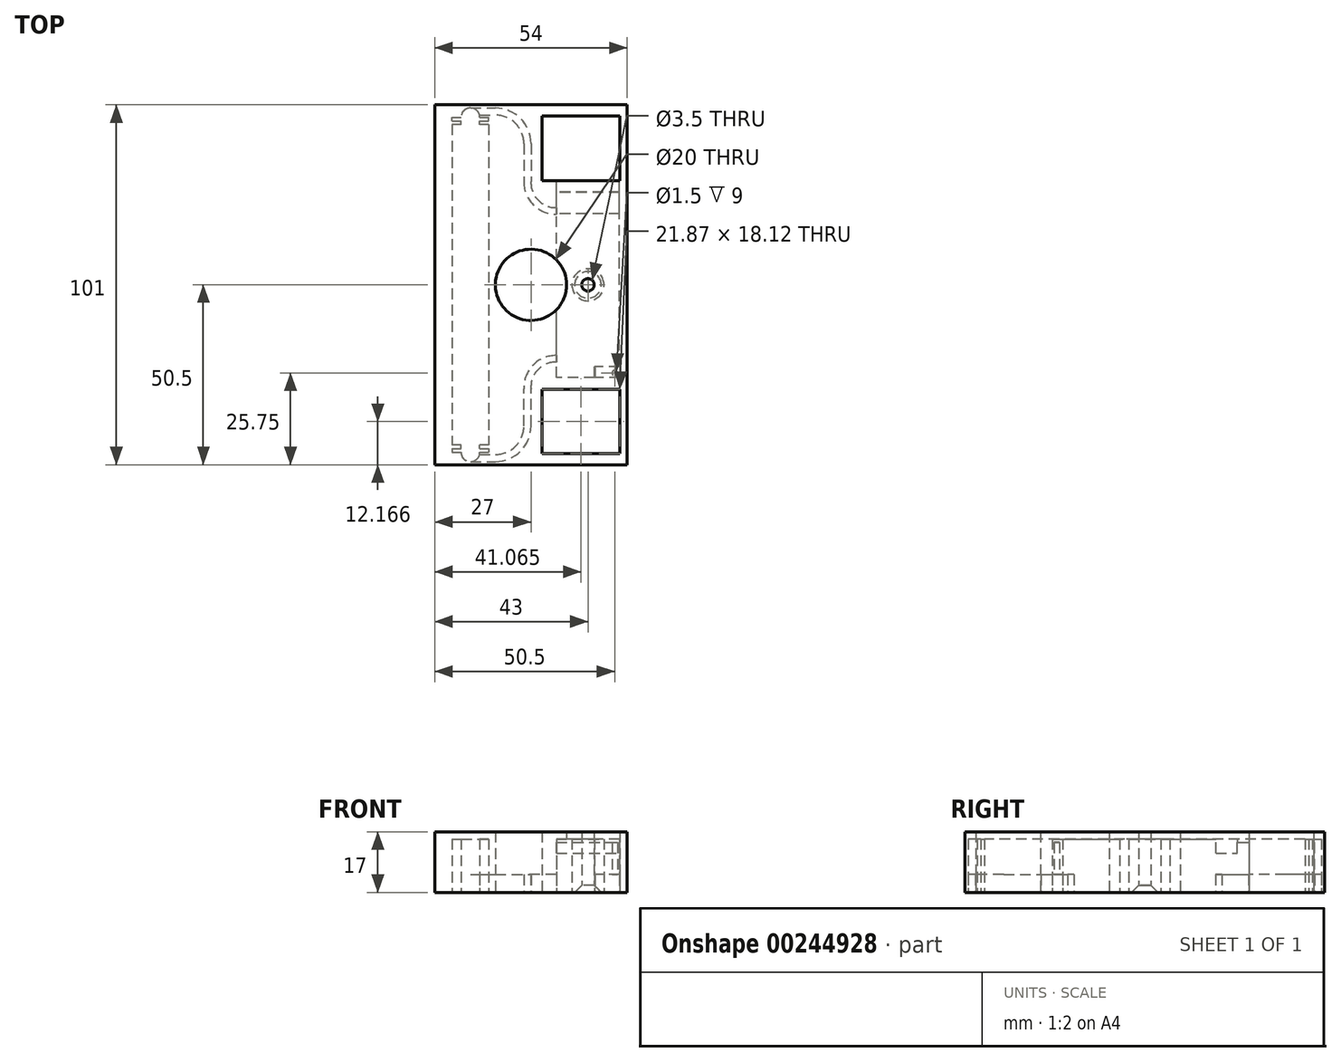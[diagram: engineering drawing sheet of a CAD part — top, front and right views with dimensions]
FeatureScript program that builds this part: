
annotation { "Feature Type Name" : "Feature", "Feature Type Description" : "" }
export const myFeature = defineFeature(function(context is Context, id is Id, definition is map)
    precondition{}
    {
        {
            var Q0;
            Q0=qCreatedBy(makeId("Top.planeOp"),FACE);
            var sketch = newSketch(context, id + "F0", { "sketchPlane" : qUnion([Q0])});
            skPoint(sketch, "E0.middle", {"position": v(0, 0) * mm});
            skLineSegment(sketch, "E1.bottom", {"start": v(27, 50.5) * mm, "end": v(-27, 50.5) * mm});
            skLineSegment(sketch, "E1.top", {"start": v(27, -50.5) * mm, "end": v(-27, -50.5) * mm});
            skLineSegment(sketch, "E1.left", {"start": v(27, 50.5) * mm, "end": v(27, -50.5) * mm});
            skLineSegment(sketch, "E2", {"start": v(-27, -50.5) * mm, "end": v(-27, 50.5) * mm});
            skLineSegment(sketch, "E3.bottom", {"start": v(25, -29.27) * mm, "end": v(3.13, -29.27) * mm});
            skLineSegment(sketch, "E3.top", {"start": v(25, -47.4) * mm, "end": v(3.13, -47.4) * mm});
            skLineSegment(sketch, "E3.left", {"start": v(25, -29.27) * mm, "end": v(25, -47.4) * mm});
            skLineSegment(sketch, "E3.right", {"start": v(3.13, -29.27) * mm, "end": v(3.13, -47.4) * mm});
            skPoint(sketch, "E3.middle", {"position": v(14.07, -38.33) * mm});
            skLineSegment(sketch, "E4", {"start": v(25, -38.33) * mm, "end": v(27, -38.33) * mm});
            skPoint(sketch, "E5.MirrorP", {"position": v(14.07, 38.33) * mm});
            skLineSegment(sketch, "E6.MirrorCS", {"start": v(25, 47.4) * mm, "end": v(3.13, 47.4) * mm});
            skLineSegment(sketch, "E7.MirrorCS", {"start": v(3.13, 29.27) * mm, "end": v(3.13, 47.4) * mm});
            skLineSegment(sketch, "E8.MirrorCS", {"start": v(25, 29.27) * mm, "end": v(3.13, 29.27) * mm});
            skLineSegment(sketch, "E9.MirrorCS", {"start": v(25, 29.27) * mm, "end": v(25, 47.4) * mm});
            skCircle(sketch, "E10", {"center": v(0, 0) * mm, "radius": 10 * mm});
            skLineSegment(sketch, "E11", {"start": v(0, 0) * mm, "end": v(16, 0) * mm});
            skCircle(sketch, "E12", {"center": v(16, 0) * mm, "radius": 1.75 * mm});
            skLineSegment(sketch, "E13", {"start": v(0, -15) * mm, "end": v(2, -15) * mm});
            skSolve(sketch);
        }
        {
            var Q0;
            Q0 = qSketchRegion(id + "F0", true);
            extrude(context, id + "F1", {"entities" : qUnion([Q0]), "depth" : 17 * mm});
        }
        {
            var Q0;
            Q0=makeQuery(id+"F1.opExtrude","CAP_FACE",FACE,{"disambiguationData":[OSD([sQuery(id+"F0.wireOp",EDGE,"E1.bottom"),sQuery(id+"F0.wireOp",EDGE,"E1.top"),sQuery(id+"F0.wireOp",EDGE,"E1.left"),sQuery(id+"F0.wireOp",EDGE,"E1.right")])],"isStart":true});
            var sketch = newSketch(context, id + "F2", { "sketchPlane" : qUnion([Q0])});
            skLineSegment(sketch, "E14", {"start": v(0, 0) * mm, "end": v(16, 0) * mm});
            skLineSegment(sketch, "E15.bottom", {"start": v(17.87, 26) * mm, "end": v(7.12, 26) * mm});
            skLineSegment(sketch, "E15.top", {"start": v(24.87, -26) * mm, "end": v(7.13, -26) * mm});
            skLineSegment(sketch, "E15.left", {"start": v(24.87, 23) * mm, "end": v(24.87, -26) * mm});
            skPoint(sketch, "E15.middle", {"position": v(16, 0) * mm});
            skCircle(sketch, "E16", {"center": v(16, 0) * mm, "radius": 4.5 * mm});
            skLineSegment(sketch, "E17.top", {"start": v(24.87, 23) * mm, "end": v(17.87, 23) * mm});
            skLineSegment(sketch, "E17.right", {"start": v(17.87, 26) * mm, "end": v(17.87, 23) * mm});
            skPoint(sketch, "E17.left.start.orphan", {"position": v(24.87, 26) * mm});
            skLineSegment(sketch, "E18.bottom", {"start": v(-11.86, -45) * mm, "end": v(-14.36, -45) * mm});
            skLineSegment(sketch, "E18.top", {"start": v(-11.86, 45) * mm, "end": v(-14.36, 45) * mm});
            skLineSegment(sketch, "E18.left", {"start": v(-11.86, -45) * mm, "end": v(-11.86, 45) * mm});
            skLineSegment(sketch, "E18.right", {"start": v(-22.14, -45) * mm, "end": v(-22.14, 45) * mm});
            skPoint(sketch, "E18.middle", {"position": v(-17, 0) * mm});
            skLineSegment(sketch, "E19", {"start": v(0, 0) * mm, "end": v(-17, 0) * mm});
            skPoint(sketch, "E20.middle", {"position": v(-17, 45) * mm});
            skLineSegment(sketch, "E21.bottom", {"start": v(-22.14, 46) * mm, "end": v(-19.64, 46) * mm});
            skLineSegment(sketch, "E21.top", {"start": v(-22.14, 47) * mm, "end": v(-19.64, 47) * mm});
            skLineSegment(sketch, "E21.left", {"start": v(-22.14, 46) * mm, "end": v(-22.14, 47) * mm});
            skLineSegment(sketch, "E21.right", {"start": v(-11.84, 46) * mm, "end": v(-11.84, 47) * mm});
            skArc(sketch, "E22", {"start": v(-14.36, 47) * mm, "mid": v(-17, 49.64) * mm, "end": v(-19.64, 47) * mm});
            skLineSegment(sketch, "E23.trimOffspring", {"start": v(-19.64, 45) * mm, "end": v(-22.14, 45) * mm});
            skLineSegment(sketch, "E24.trimOffspring", {"start": v(-14.36, 46) * mm, "end": v(-11.84, 46) * mm});
            skLineSegment(sketch, "E25.trimOffspring", {"start": v(-14.36, 47) * mm, "end": v(-11.84, 47) * mm});
            skLineSegment(sketch, "E26.MirrorCS", {"start": v(-14.36, -45) * mm, "end": v(-14.36, -46) * mm});
            skLineSegment(sketch, "E27.MirrorCS", {"start": v(-19.64, -45) * mm, "end": v(-19.64, -46) * mm});
            skLineSegment(sketch, "E28.MirrorCS", {"start": v(-22.14, -46) * mm, "end": v(-19.64, -46) * mm});
            skLineSegment(sketch, "E29.MirrorCS", {"start": v(-22.14, -46) * mm, "end": v(-22.14, -47) * mm});
            skLineSegment(sketch, "E30.MirrorCS", {"start": v(-22.14, -47) * mm, "end": v(-19.64, -47) * mm});
            skArc(sketch, "E31.MirrorCS", {"start": v(-14.36, -47) * mm, "mid": v(-17, -49.64) * mm, "end": v(-19.64, -47) * mm});
            skLineSegment(sketch, "E32.MirrorCS", {"start": v(-14.36, -47) * mm, "end": v(-11.84, -47) * mm});
            skLineSegment(sketch, "E33.MirrorCS", {"start": v(-11.84, -46) * mm, "end": v(-11.84, -47) * mm});
            skLineSegment(sketch, "E34.MirrorCS", {"start": v(-14.36, -46) * mm, "end": v(-11.84, -46) * mm});
            skLineSegment(sketch, "E35", {"start": v(7.12, 26) * mm, "end": v(7.13, -26) * mm});
            skLineSegment(sketch, "E36.trimOffspring", {"start": v(-19.64, -45) * mm, "end": v(-22.14, -45) * mm});
            skLineSegment(sketch, "E37", {"start": v(-19.64, 46) * mm, "end": v(-19.64, 45) * mm});
            skLineSegment(sketch, "E38", {"start": v(-14.36, 46) * mm, "end": v(-14.36, 45) * mm});
            skSolve(sketch);
        }
        {
            var Q0;
            Q0 = qSketchRegion(id + "F2", true);
            extrude(context, id + "F3", {"entities" : qUnion([Q0]), "operationType" : NewBodyOperationType.REMOVE, "oppositeDirection" : true, "depth" : 15 * mm});
        }
        {
            var Q0;
            {var subQ5=sQuery(id+"F0.wireOp",EDGE,"E1.top");var subQ6=sQuery(id+"F0.wireOp",EDGE,"E1.right");var subQ7=sQuery(id+"F0.wireOp",EDGE,"E1.bottom");var subQ8=sQuery(id+"F0.wireOp",EDGE,"E1.left");Q0=makeQuery(id+"F3.boolean.opBoolean","SPLIT",FACE,{"disambiguationData":[TD([makeQuery(id+"F1.opExtrude","SWEPT_FACE",FACE,{"disambiguationData":[OSD([subQ7])]})])],"derivedFrom":makeQuery(id+"F1.opExtrude","CAP_FACE",FACE,{"disambiguationData":[OSD([subQ7,subQ5,subQ8,subQ6])],"isStart":true})});}
            var sketch = newSketch(context, id + "F4", { "sketchPlane" : qUnion([Q0])});
            skLineSegment(sketch, "E39.bottom", {"start": v(25, 23) * mm, "end": v(18, 23) * mm});
            skLineSegment(sketch, "E39.top", {"start": v(25, 26) * mm, "end": v(18, 26) * mm});
            skLineSegment(sketch, "E39.left", {"start": v(25, 23) * mm, "end": v(25, 26) * mm});
            skLineSegment(sketch, "E39.right", {"start": v(18, 23) * mm, "end": v(18, 26) * mm});
            skPoint(sketch, "E39.middle", {"position": v(21.5, 24.5) * mm});
            skPoint(sketch, "E40.startSnap0", {"position": v(-17, 49.64) * mm});
            skArc(sketch, "E41", {"start": v(0, 39.62) * mm, "mid": v(-2.93, 46.7) * mm, "end": v(-10, 49.62) * mm});
            skArc(sketch, "E42", {"start": v(0, 29.13) * mm, "mid": v(1.92, 23.83) * mm, "end": v(7.12, 21.66) * mm});
            skLineSegment(sketch, "E43", {"start": v(0, 39.62) * mm, "end": v(0, 29.13) * mm});
            skLineSegment(sketch, "E44", {"start": v(-2, 39.62) * mm, "end": v(-2, 29.13) * mm});
            skArc(sketch, "E45", {"start": v(-2, 29.13) * mm, "mid": v(0.58, 22.52) * mm, "end": v(7.16, 19.84) * mm});
            skPoint(sketch, "E46.MirrorP", {"position": v(-17, -49.64) * mm});
            skLineSegment(sketch, "E47", {"start": v(7.12, 21.66) * mm, "end": v(7.16, 19.84) * mm});
            skLineSegment(sketch, "E48", {"start": v(-17, 49.64) * mm, "end": v(-10, 49.62) * mm});
            skLineSegment(sketch, "E49", {"start": v(-10, 49.62) * mm, "end": v(0, 49.62) * mm});
            skLineSegment(sketch, "E50", {"start": v(-17, 49.64) * mm, "end": v(-17, 47.64) * mm});
            skLineSegment(sketch, "E51", {"start": v(-17, 47.64) * mm, "end": v(-10, 47.64) * mm});
            skArc(sketch, "E52", {"start": v(-2, 39.62) * mm, "mid": v(-4.34, 45.29) * mm, "end": v(-10, 47.64) * mm});
            skArc(sketch, "E53.MirrorCS", {"start": v(-2, -29.13) * mm, "mid": v(0.58, -22.52) * mm, "end": v(7.16, -19.84) * mm});
            skArc(sketch, "E54.MirrorCS", {"start": v(0, -29.13) * mm, "mid": v(1.92, -23.83) * mm, "end": v(7.12, -21.66) * mm});
            skLineSegment(sketch, "E55.MirrorCS", {"start": v(-2, -39.62) * mm, "end": v(-2, -29.13) * mm});
            skLineSegment(sketch, "E56.MirrorCS", {"start": v(0, -39.62) * mm, "end": v(0, -29.13) * mm});
            skArc(sketch, "E57.MirrorCS", {"start": v(0, -39.62) * mm, "mid": v(-2.93, -46.7) * mm, "end": v(-10, -49.62) * mm});
            skArc(sketch, "E58.MirrorCS", {"start": v(-2, -39.62) * mm, "mid": v(-4.34, -45.29) * mm, "end": v(-10, -47.64) * mm});
            skLineSegment(sketch, "E59.MirrorCS", {"start": v(-17, -47.64) * mm, "end": v(-10, -47.64) * mm});
            skLineSegment(sketch, "E60.MirrorCS", {"start": v(-17, -49.64) * mm, "end": v(-10, -49.62) * mm});
            skLineSegment(sketch, "E61.MirrorCS", {"start": v(-17, -49.64) * mm, "end": v(-17, -47.64) * mm});
            skLineSegment(sketch, "E62.MirrorCS", {"start": v(7.13, -21.66) * mm, "end": v(7.16, -19.84) * mm});
            skSolve(sketch);
        }
        {
            var Q0;
            Q0 = qSketchRegion(id + "F4", true);
            extrude(context, id + "F5", {"entities" : qUnion([Q0]), "operationType" : NewBodyOperationType.REMOVE, "oppositeDirection" : true, "depth" : 5 * mm});
        }
        {
            var Q0;
            Q0=makeQuery(id+"F3.boolean.opBoolean","SPLIT",FACE,{"disambiguationData":[TD([makeQuery(id+"F3.opExtrude","SWEPT_FACE",FACE,{"disambiguationData":[OSD([sQuery(id+"F2.wireOp",EDGE,"E16")])]})])],"derivedFrom":makeQuery(id+"F1.opExtrude","CAP_FACE",FACE,{"disambiguationData":[OSD([sQuery(id+"F0.wireOp",EDGE,"E1.bottom"),sQuery(id+"F0.wireOp",EDGE,"E1.top"),sQuery(id+"F0.wireOp",EDGE,"E1.left"),sQuery(id+"F0.wireOp",EDGE,"E1.right")])],"isStart":true})});
            var sketch = newSketch(context, id + "F6", { "sketchPlane" : qUnion([Q0])});
            skLineSegment(sketch, "E63", {"start": v(0, 0) * mm, "end": v(16, 0) * mm});
            skLineSegment(sketch, "E64", {"start": v(0, 0) * mm, "end": v(0, 24.75) * mm});
            skLineSegment(sketch, "E65", {"start": v(0, 24.75) * mm, "end": v(23.5, 24.75) * mm});
            skCircle(sketch, "E66", {"center": v(23.5, 24.75) * mm, "radius": 0.75 * mm});
            skLineSegment(sketch, "E67.bottom", {"start": v(7.12, -26) * mm, "end": v(24.87, -26) * mm});
            skLineSegment(sketch, "E67.top", {"start": v(7.12, -47.5) * mm, "end": v(24.88, -47.5) * mm});
            skLineSegment(sketch, "E67.left", {"start": v(7.12, -26) * mm, "end": v(7.12, -47.5) * mm});
            skLineSegment(sketch, "E67.right", {"start": v(24.87, -26) * mm, "end": v(24.87, -47.5) * mm});
            skLineSegment(sketch, "E68", {"start": v(0, 0) * mm, "end": v(0, -36.75) * mm});
            skPoint(sketch, "E68.endSnap0", {"position": v(7.12, -36.75) * mm});
            skLineSegment(sketch, "E69", {"start": v(0, -36.75) * mm, "end": v(16, -36.75) * mm});
            skPoint(sketch, "E69.endSnap0", {"position": v(16, -47.5) * mm});
            skSolve(sketch);
        }
        {
            var Q0;
            Q0 = qSketchRegion(id + "F6", true);
            extrude(context, id + "F7", {"entities" : qUnion([Q0]), "operationType" : NewBodyOperationType.REMOVE, "oppositeDirection" : true, "depth" : 14 * mm});
        }
        {
            var Q0;
            Q0=makeQuery(id+"F1.opExtrude","CAP_EDGE",EDGE,{"disambiguationData":[OSD([sQuery(id+"F0.wireOp",EDGE,"Qu2J6p73-t3Vd-1OHA-CPek-KJU0flgLsV9Q")])],"isStart":true});
            var Q1;
            Q1=makeQuery(id+"F1.opExtrude","CAP_EDGE",EDGE,{"disambiguationData":[OSD([sQuery(id+"F0.wireOp",EDGE,"E12")])],"isStart":true});
            var Q2;
            Q2=makeQuery(id+"F1.opExtrude","CAP_EDGE",EDGE,{"disambiguationData":[OSD([sQuery(id+"F0.wireOp",EDGE,"fec9e059-fcf4-4ae0-b975-56ffe9dcbc380.MirrorC")])],"isStart":true});
            chamfer(context, id + "F8", {"entities" : qUnion([Q0, Q1, Q2]), "width" : 2 * mm, "tangentPropagation" : true});
        }
        {
            var Q0;
            Q0=makeQuery(id+"F1.opExtrude","CAP_FACE",FACE,{"disambiguationData":[OSD([sQuery(id+"F0.wireOp",EDGE,"E1.bottom"),sQuery(id+"F0.wireOp",EDGE,"E1.top"),sQuery(id+"F0.wireOp",EDGE,"E1.left"),sQuery(id+"F0.wireOp",EDGE,"E2"),sQuery(id+"F0.wireOp",EDGE,"E3.bottom"),sQuery(id+"F0.wireOp",EDGE,"E3.top"),sQuery(id+"F0.wireOp",EDGE,"E3.left"),sQuery(id+"F0.wireOp",EDGE,"E3.right"),sQuery(id+"F0.wireOp",EDGE,"E6.MirrorCS"),sQuery(id+"F0.wireOp",EDGE,"E7.MirrorCS"),sQuery(id+"F0.wireOp",EDGE,"E8.MirrorCS"),sQuery(id+"F0.wireOp",EDGE,"E9.MirrorCS"),sQuery(id+"F0.wireOp",EDGE,"E10"),sQuery(id+"F0.wireOp",EDGE,"E12")])],"isStart":false});
            var sketch = newSketch(context, id + "F9", { "sketchPlane" : qUnion([Q0])});
            skLineSegment(sketch, "E70.bottom", {"start": v(7.04, 19.97) * mm, "end": v(25.04, 19.97) * mm});
            skLineSegment(sketch, "E70.top", {"start": v(7.04, 25.97) * mm, "end": v(25.04, 25.97) * mm});
            skLineSegment(sketch, "E70.left", {"start": v(7.04, 19.97) * mm, "end": v(7.04, 25.97) * mm});
            skLineSegment(sketch, "E70.right", {"start": v(25.04, 19.97) * mm, "end": v(25.04, 25.97) * mm});
            skSolve(sketch);
        }
        {
            var Q0;
            Q0 = qSketchRegion(id + "F9", true);
            extrude(context, id + "F10", {"entities" : qUnion([Q0]), "operationType" : NewBodyOperationType.ADD, "oppositeDirection" : true, "depth" : 6 * mm});
        }
    });
